# Revit family: CA6005551_Toallero Barra
name_source: partatom
category: Furniture
units: mm (PartAtom-declared; Revit-internal decimal feet)

## family parameters
Always vertical = Yes
Cut with Voids When Loaded = No
Host = Wall
OmniClass Number = 23.31.25.25
OmniClass Title = Towel Bars
Room Calculation Point = No
Shared = No

## types (1)
- Type 1
    Alto = 47 mm  [stored 0.154199 ft]
    Altura = 900 mm  [stored 2.95276 ft]
    Ancho = 533 mm  [stored 1.74869 ft]
    Creado por = IDD
    Description = La línea de griferías y accesorios plásticos Cascade se inspira en la fluidez natural
del agua y en las formas creadas a su paso en caídas y cascadas, los gestos de
diseño y formas de Cascade invitan al usuario al uso, sus líneas fluidas crean un
solo viaje alrededor del producto generando formas limpias.
    Dimensiónes generales producto empacado Kit x6 = (H x L x W): 441 x 160 x 79 mm.
    Fecha de creación = 10/08/2020
    Garantía = 30 Años
    Garantía Acabados = 5 Años
    Manufacturer = Corona
    Material = Corona_Cromado
    Peso Neto aprox = 9 Kg
    Peso neto = 470 g. - 1,04 lb.
    Profundidad = 71 mm  [stored 0.23294 ft]
    Referencia = CA6005551
    Temperatura de uso = 4˚C a 40˚C.
    URL = https://corona.co

note: [stored X ft] marks values corroborated as IEEE doubles in the binary element streams (Revit-internal decimal feet)

## geometry (parser evidence)
native form markers: Sweep x7
no freeform markers — native parametric forms only
